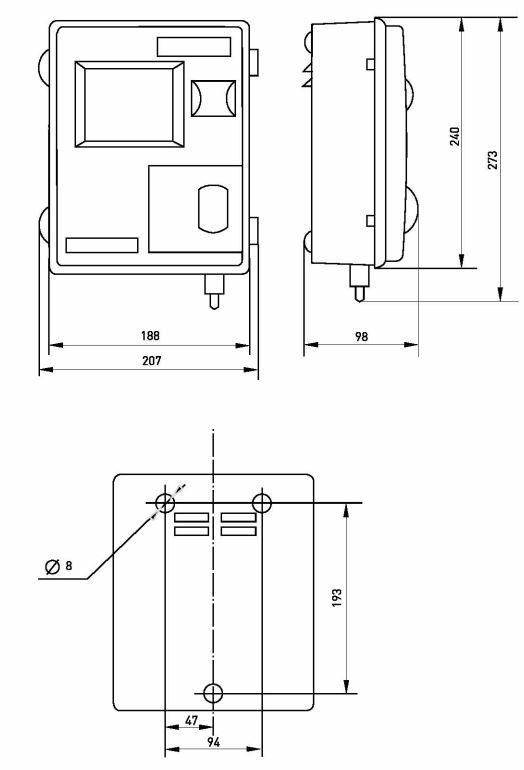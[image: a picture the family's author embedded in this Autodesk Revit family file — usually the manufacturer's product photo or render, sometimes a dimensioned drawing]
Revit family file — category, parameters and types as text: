
# Revit family: EKF_EE_ЩУ-П_IP54_PROxima
name_source: partatom
category: Электрооборудование
units: mm (PartAtom-declared; Revit-internal decimal feet)

## family parameters
Всегда вертикально = Да
На основе рабочей плоскости = Нет
Общий = Нет
При загрузке вырезать с полостями = Нет
Размер круглого соединителя = Использовать диаметр
Тип детали = Силовой щит
Точка расчета площади = Да

## types (1)
- ЩУ-П IP54 EKF PROxima
    ADSK_Единица измерения = компл.
    ADSK_Завод-изготовитель = EKF
    ADSK_Классификация нагрузок = Прочее
    ADSK_Код изделия = pb-y-54
    ADSK_Количество = 1
    ADSK_Количество фаз = 1
    ADSK_Коэффициент мощности = 1
    ADSK_Марка = ЩУ-П IP54
    ADSK_Масса = 0.85
    ADSK_Материал = Белый_ABS-пластик
    ADSK_Наименование = Щит учетный пластиковый ЩУ-П IP54 EKF PROxima
    ADSK_Напряжение = 400 В
    ADSK_Номинальная мощность = 0 Вт
    ADSK_Обозначение = ЩУ-П IP54
    ADSK_Полная мощность = 0 В·А
    ADSK_Размер_Высота = 239 мм
    ADSK_Размер_Глубина = 98 мм
    ADSK_Размер_Ширина = 187 мм
    ADSK_Ток = 125 А
    Изготовитель = EKF
    Количество DIN-реек = 1
    Количество модулей на DIN-рейке = 3
    Максимальное количество модулей = 3
    Описание = Щит учетный пластиковый ЩУ-П IP54 EKF PROxima
    Серия номенклатуры = PROxima
    Степень защиты IP = IP54
    ТВ = EKF
    Тип = 8 мм
    Тип установки = Навесной
